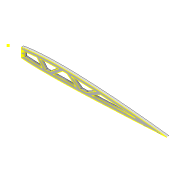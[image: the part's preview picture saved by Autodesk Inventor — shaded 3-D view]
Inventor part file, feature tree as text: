
AUTODESK INVENTOR PART (.ipt)
format: ipt  version: 2022 (Build 260153000, 153)  size: 247,296 bytes
history: native  units: mm
features: sketch x6, extrude x5, projected_geometry x3, shell x1
ambient origin geometry x8: Origin, YZ Plane, XZ Plane, XY Plane, X Axis, Y Axis, Z Axis, Center Point
bodies: Solid1 (feature_tree)
feature tree (15):
  extrude  "Extrusion1"  Depth=5.0mm
  shell  "Shell1"  Thickness=6.0mm
  extrude  "Extrusion2"  Depth=4.5mm TaperAngle=0.0deg
  extrude  "Extrusion3"  Depth=2.1mm
  extrude  "Extrusion4"  Depth=3.0mm
  extrude  "Extrusion5"  Depth=10.0mm TaperAngle=0.0deg
  sketch  "Sketch6"  dims[d15=10.0mm d16=0.0mm d17=5.0mm d18=5.0mm d19=5.0mm d20=5.0mm d21=4.5mm d22=0.0mm d24=0.4mm]
  sketch  "Sketch1"  dims[d0=4.5mm d1=0.0mm d2=5.0mm d3=6.0mm]
  sketch  "Sketch2"  dims[d4=25.0mm d5=4.5mm d6=0.0mm]
  projected_geometry  "Projected Loop1"
  sketch  "Sketch3"  dims[d7=2.1mm d8=2.1mm]
  sketch  "Sketch4"  dims[d9=7.0mm d11=3.0mm]
  sketch  "Sketch5"  dims[d12=3.0mm d13=10.0mm d14=0.0mm]
  projected_geometry  "Projected Loop2"
  projected_geometry  "Projected Loop3"
